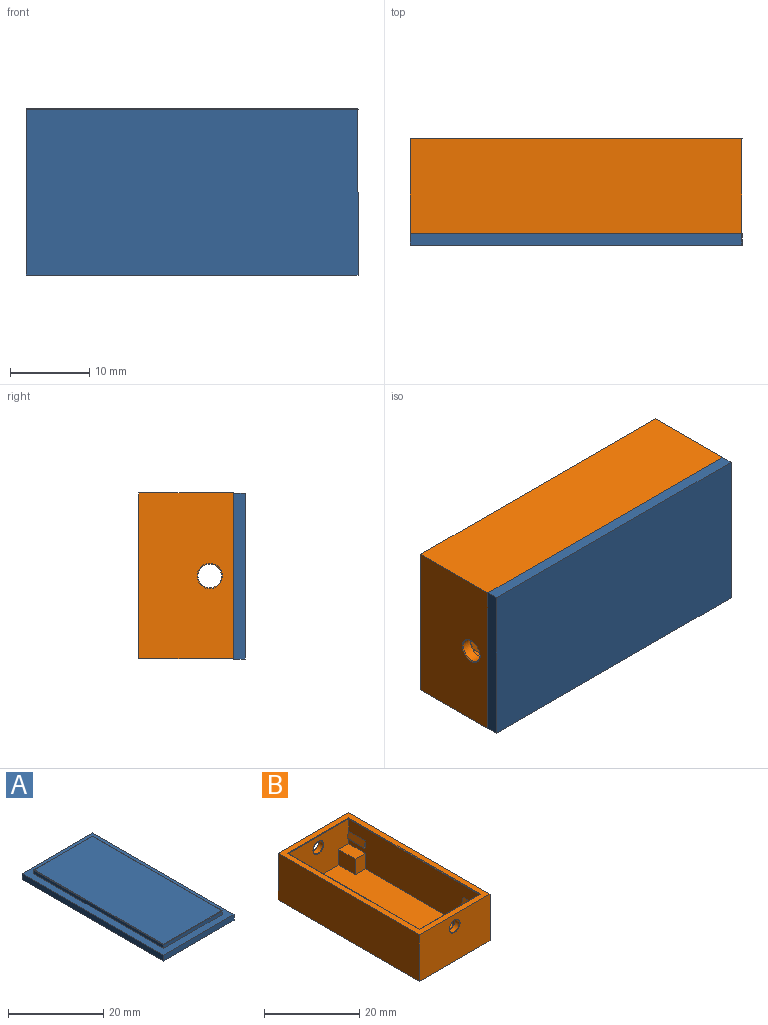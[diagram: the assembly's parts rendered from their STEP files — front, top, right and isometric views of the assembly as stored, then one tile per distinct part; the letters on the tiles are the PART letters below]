
ASSEMBLY  parts=2 mates=1
PART A: 15 faces, bbox 21x42x2.5 mm
  f0: plane 42x1.5mm, normal (-1,0,0), area 63mm2, adj f1,f3,f4,f5
  f1: plane 21x1.5mm, normal (0,-1,0), area 31.5mm2, adj f0,f2,f4,f5
  f2: plane 42x1.5mm, normal (1,0,0), area 63mm2, adj f1,f3,f4,f5
  f3: plane 21x1.5mm, normal (0,1,0), area 31.5mm2, adj f0,f2,f4,f5
  f4: plane 42x21mm, normal (0,0,1), area 208.2mm2, adj f0,f1,f2,f3,f6,f7,f8,f9
  f5: plane 42x21mm, normal (0,0,-1), area 882mm2, adj f0,f1,f2,f3
  f6: plane 38.5x0.9mm, normal (-1,0,0), area 34.6mm2, adj f4,f7,f9,f11
  f7: plane 17.5x0.9mm, normal (0,-1,0), area 15.8mm2, adj f4,f6,f8,f12
  f8: plane 38.5x0.9mm, normal (1,0,0), area 34.6mm2, adj f4,f7,f9,f14
  f9: plane 17.5x0.9mm, normal (0,1,0), area 15.8mm2, adj f4,f6,f8,f13
  f10: plane 38.3x17.3mm, normal (0,0,1), area 662.6mm2, adj f11,f12,f13,f14
  f11: cylinder r=0.1mm len=38.5mm, axis (0,1,0), area 6mm2, adj f6,f10,f12,f13
  f12: cylinder r=0.1mm len=17.5mm, axis (-1,0,0), area 2.7mm2, adj f7,f10,f11,f14
  f13: cylinder r=0.1mm len=17.5mm, axis (1,0,0), area 2.7mm2, adj f9,f10,f11,f14
  f14: cylinder r=0.1mm len=38.5mm, axis (0,-1,0), area 6mm2, adj f8,f10,f12,f13
PART B: 53 faces, bbox 21x42x12 mm
  f0: plane 18x10.4mm, normal (0,1,0), area 154.3mm2, adj f1,f2,f4,f17,f19,f20,f21,f30
  f1: plane 39x18mm, normal (0,0,1), area 642mm2, adj f0,f2,f3,f4,f11,f12,f17,f18
  f2: plane 39x10.4mm, normal (-1,0,0), area 347.7mm2, adj f0,f1,f3,f23,f25,f27,f28,f29
  f3: plane 18x10.4mm, normal (0,-1,0), area 154.3mm2, adj f1,f2,f4,f11,f13,f14,f15,f23
  f4: plane 39x10.4mm, normal (1,0,0), area 347.7mm2, adj f0,f1,f3,f12,f13,f15,f16,f18
  f5: plane 42x12mm, normal (-1,0,0), area 504mm2, adj f6,f8,f9,f10
  f6: plane 21x12mm, normal (0,-1,0), area 244mm2, adj f5,f7,f9,f10,f40
  f7: plane 42x12mm, normal (1,0,0), area 504mm2, adj f6,f8,f9,f10
  f8: plane 21x12mm, normal (0,1,0), area 244mm2, adj f5,f7,f9,f10,f39
  f9: plane 42x21mm, normal (0,0,1), area 168.6mm2, adj f5,f6,f7,f8,f49,f50,f51,f52
  f10: plane 42x21mm, normal (0,0,-1), area 882mm2, adj f5,f6,f7,f8
  f11: plane 5x4mm, normal (1,0,0), area 20mm2, adj f1,f3,f12,f13
  f12: plane 4x3mm, normal (0,-1,0), area 12mm2, adj f1,f4,f11,f13
  f13: plane 5x3mm, normal (0,0,1), area 15mm2, adj f3,f4,f11,f12
  f14: plane 5x0.27mm, normal (0,0,-1), area 1.3mm2, adj f3,f16,f47,f48
  f15: plane 5x1.56mm, normal (0.96,0,0.28), area 8.2mm2, adj f3,f4,f16,f47
  f16: plane 1.79x0.47mm, normal (0,-1,0), area 0.4mm2, adj f4,f14,f15,f47,f48
  f17: plane 5x4mm, normal (1,0,0), area 20mm2, adj f0,f1,f18,f19
  f18: plane 4x3mm, normal (0,1,0), area 12mm2, adj f1,f4,f17,f19
  f19: plane 5x3mm, normal (0,0,1), area 15mm2, adj f0,f4,f17,f18
  f20: plane 5x0.27mm, normal (0,0,-1), area 1.3mm2, adj f0,f22,f45,f46
  f21: plane 5x1.56mm, normal (0.96,0,0.28), area 8.2mm2, adj f0,f4,f22,f45
  f22: plane 1.79x0.47mm, normal (0,1,0), area 0.4mm2, adj f4,f20,f21,f45,f46
  f23: plane 5x3mm, normal (0,0,1), area 15mm2, adj f2,f3,f24,f25
  f24: plane 5x4mm, normal (-1,0,0), area 20mm2, adj f1,f3,f23,f25
  f25: plane 4x3mm, normal (0,-1,0), area 12mm2, adj f1,f2,f23,f24
  f26: plane 5x0.27mm, normal (0,0,-1), area 1.3mm2, adj f3,f28,f43,f44
  f27: plane 5x1.56mm, normal (-0.96,0,0.28), area 8.2mm2, adj f2,f3,f28,f43
  f28: plane 1.79x0.47mm, normal (0,-1,0), area 0.4mm2, adj f2,f26,f27,f43,f44
  f29: plane 4x3mm, normal (0,1,0), area 12mm2, adj f1,f2,f30,f31
  f30: plane 5x4mm, normal (-1,0,0), area 20mm2, adj f0,f1,f29,f31
  f31: plane 5x3mm, normal (0,0,1), area 15mm2, adj f0,f2,f29,f30
  f32: plane 5x0.27mm, normal (0,0,-1), area 1.3mm2, adj f0,f34,f41,f42
  f33: plane 5x1.56mm, normal (-0.96,0,0.28), area 8.2mm2, adj f0,f2,f34,f41
  f34: plane 1.79x0.47mm, normal (0,1,0), area 0.4mm2, adj f2,f32,f33,f41,f42
  f35: cylinder r=1.5mm len=3mm, axis (0,-1,0), area 12.3mm2, adj f38,f39
  f36: cylinder r=1.5mm len=3mm, axis (0,-1,0), area 12.3mm2, adj f37,f40
  f37: torus R=1.6mm, axis (0,1,0), area 1.5mm2, adj f0,f36
  f38: torus R=1.6mm, axis (0,1,0), area 1.5mm2, adj f3,f35
  f39: torus R=1.6mm, axis (0,1,0), area 1.5mm2, adj f8,f35
  f40: torus R=1.6mm, axis (0,1,0), area 1.5mm2, adj f6,f36
  f41: cylinder r=0.1mm len=5mm, axis (0,1,0), area 0.9mm2, adj f0,f32,f33,f34
  f42: cylinder r=0.1mm len=5mm, axis (0,1,0), area 0.8mm2, adj f0,f2,f32,f34
  f43: cylinder r=0.1mm len=5mm, axis (0,-1,0), area 0.9mm2, adj f3,f26,f27,f28
  f44: cylinder r=0.1mm len=5mm, axis (0,1,0), area 0.8mm2, adj f2,f3,f26,f28
  f45: cylinder r=0.1mm len=5mm, axis (0,1,0), area 0.9mm2, adj f0,f20,f21,f22
  f46: cylinder r=0.1mm len=5mm, axis (0,1,0), area 0.8mm2, adj f0,f4,f20,f22
  f47: cylinder r=0.1mm len=5mm, axis (0,-1,0), area 0.9mm2, adj f3,f14,f15,f16
  f48: cylinder r=0.1mm len=5mm, axis (0,1,0), area 0.8mm2, adj f3,f4,f14,f16
  f49: cylinder r=0.1mm len=39.2mm, axis (0,1,0), area 6.1mm2, adj f2,f9,f50,f51
  f50: cylinder r=0.1mm len=18.2mm, axis (-1,0,0), area 2.8mm2, adj f3,f9,f49,f52
  f51: cylinder r=0.1mm len=18.2mm, axis (1,0,0), area 2.8mm2, adj f0,f9,f49,f52
  f52: cylinder r=0.1mm len=39.2mm, axis (0,-1,0), area 6.1mm2, adj f4,f9,f50,f51
PLACE A rot(axis=(-0.58,0.58,0.58),120deg) t=(21,-7.5,44.32)mm
PLACE B rot(axis=(0.58,0.58,-0.58),120deg) t=(21,6,17.25)mm
MATE planar A.f4 <-> B.f9  axis (0,1,0) through (21,-6,17.25)mm
